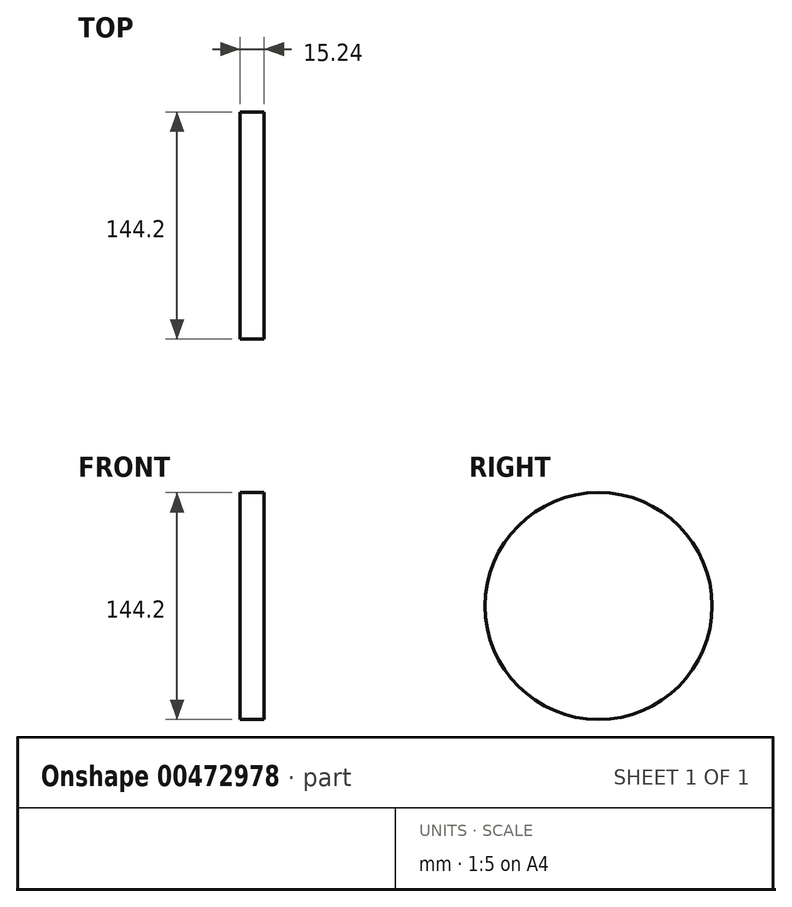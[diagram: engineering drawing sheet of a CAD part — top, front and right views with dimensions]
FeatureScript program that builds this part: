
annotation { "Feature Type Name" : "Feature", "Feature Type Description" : "" }
export const myFeature = defineFeature(function(context is Context, id is Id, definition is map)
    precondition{}
    {
        {
            var Q0;
            Q0=qCreatedBy(makeId("Right.planeOp"),FACE);
            var sketch = newSketch(context, id + "F0", { "sketchPlane" : qUnion([Q0])});
            skCircle(sketch, "E0", {"center": v(0, 0) * mm, "radius": 72.1 * mm});
            skSolve(sketch);
        }
        {
            var Q0;
            Q0=makeQuery(id+"F0.imprint","IMPRINT",FACE,{"disambiguationData":[TD([[makeQuery(id+"F0.imprint","IMPRINT",EDGE,{"derivedFrom":sQuery(id+"F0.wireOp",EDGE,"E0")}),1.0]])]});
            extrude(context, id + "F1", {"entities" : qUnion([Q0]), "depth" : 15.24 * mm});
        }
        {
            var Q0;
            Q0=makeQuery(id+"F1.opExtrude","CAP_FACE",FACE,{"disambiguationData":[OSD([sQuery(id+"F0.wireOp",EDGE,"E0")])],"isStart":false});
            var sketch = newSketch(context, id + "F2", { "sketchPlane" : qUnion([Q0])});
            skLineSegment(sketch, "E1", {"start": v(0, -19.33) * mm, "end": v(0, 18.34) * mm});
            skFitSpline(sketch, "E2", {"points": [v(0, -19.33) * mm, v(20.28, -4.2) * mm, v(28.8, 25.21) * mm, v(18.63, 34.56) * mm, v(0, 18.34) * mm], "startDerivative": vector(83.73, 43.91) * mm, "endDerivative": vector(-73.44, -91.93) * mm});
            skFitSpline(sketch, "E3.MirrorCS", {"points": [v(0, -19.33) * mm, v(-20.28, -4.2) * mm, v(-28.8, 25.21) * mm, v(-18.63, 34.56) * mm, v(0, 18.34) * mm], "startDerivative": vector(-83.73, 43.91) * mm, "endDerivative": vector(73.44, -91.93) * mm});
            skSolve(sketch);
        }
        {
            var Q0;
            Q0=makeQuery(id+"F2.imprint","IMPRINT",FACE,{"disambiguationData":[TD([[makeQuery(id+"F2.imprint","IMPRINT",EDGE,{"derivedFrom":sQuery(id+"F2.wireOp",EDGE,"E2")}),-1.0]])]});
            var sketch = newSketch(context, id + "F3", { "sketchPlane" : qUnion([Q0])});
            skLineSegment(sketch, "E4.bottom", {"start": v(-37.72, 61.15) * mm, "end": v(37.72, 61.15) * mm});
            skLineSegment(sketch, "E4.top", {"start": v(-37.72, -61.15) * mm, "end": v(37.72, -61.15) * mm});
            skLineSegment(sketch, "E4.left", {"start": v(-37.72, 61.15) * mm, "end": v(-37.72, -61.15) * mm});
            skLineSegment(sketch, "E4.right", {"start": v(37.72, 61.15) * mm, "end": v(37.72, -61.15) * mm});
            skPoint(sketch, "E4.middle", {"position": v(0, 0) * mm});
            skSolve(sketch);
        }
        {
            var Q0;
            Q0=makeQuery(id+"F2.imprint","IMPRINT",FACE,{"disambiguationData":[TD([[makeQuery(id+"F2.imprint","IMPRINT",EDGE,{"derivedFrom":sQuery(id+"F2.wireOp",EDGE,"E2")}),-1.0]])]});
            var Q1;
            Q1 = qSketchRegion(id + "F3", true);
            extrude(context, id + "F4", {"entities" : qUnion([Q0, Q1]), "operationType" : NewBodyOperationType.ADD, "oppositeDirection" : true, "depth" : 3.8 * mm});
        }
    });
